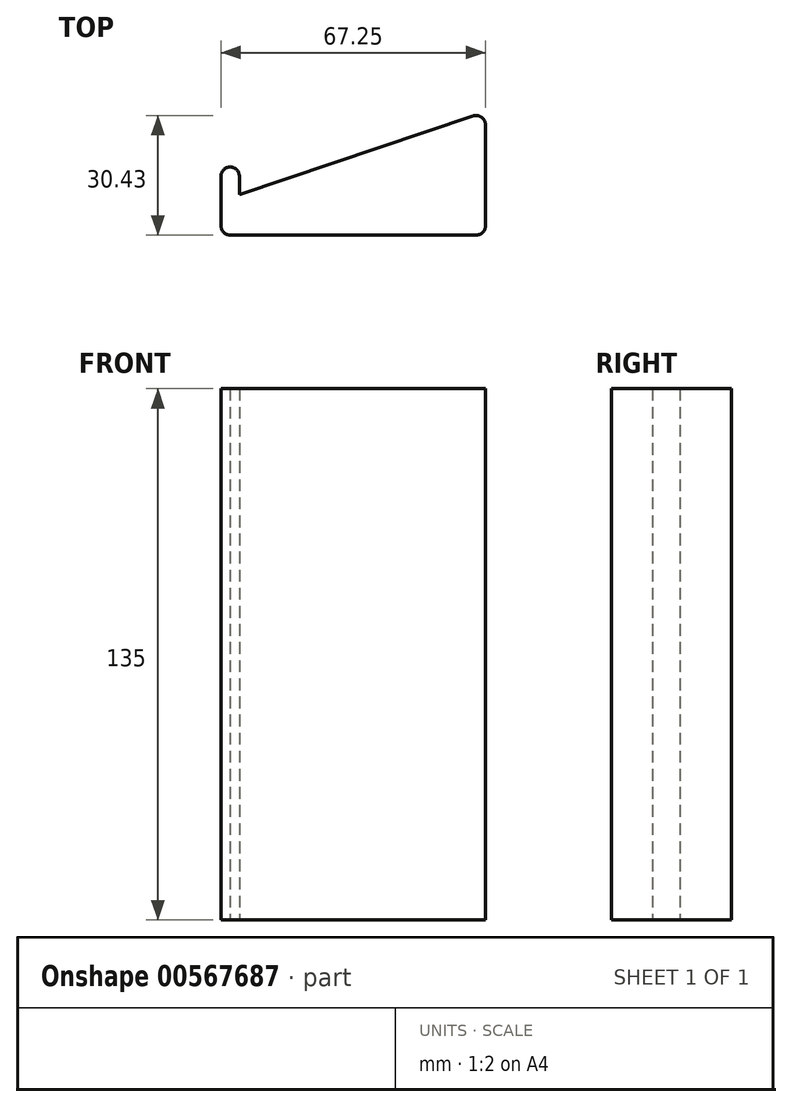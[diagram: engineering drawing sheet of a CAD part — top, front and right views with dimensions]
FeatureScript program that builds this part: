
annotation { "Feature Type Name" : "Feature", "Feature Type Description" : "" }
export const myFeature = defineFeature(function(context is Context, id is Id, definition is map)
    precondition{}
    {
        {
            var Q0;
            Q0=qCreatedBy(makeId("Top.planeOp"),FACE);
            var sketch = newSketch(context, id + "F0", { "sketchPlane" : qUnion([Q0])});
            skLineSegment(sketch, "E0", {"start": v(-28.86, 54.66) * mm, "end": v(30.37, 74.6) * mm});
            skLineSegment(sketch, "E1", {"start": v(33.67, 72.24) * mm, "end": v(33.67, 46.8) * mm});
            skLineSegment(sketch, "E2", {"start": v(31.17, 44.3) * mm, "end": v(-31.08, 44.3) * mm});
            skLineSegment(sketch, "E3", {"start": v(-33.58, 46.8) * mm, "end": v(-33.58, 59.2) * mm});
            skLineSegment(sketch, "E4", {"start": v(-31.36, 61.7) * mm, "end": v(-31.08, 61.7) * mm});
            skLineSegment(sketch, "E5", {"start": v(-28.86, 59.2) * mm, "end": v(-28.86, 54.66) * mm});
            skPoint(sketch, "E6.visualSharp", {"position": v(-28.86, 61.7) * mm});
            skArc(sketch, "E6.filletArc", {"start": v(-28.86, 59.2) * mm, "mid": v(-29.6, 60.96) * mm, "end": v(-31.36, 61.7) * mm});
            skPoint(sketch, "E7.visualSharp", {"position": v(33.67, 75.72) * mm});
            skArc(sketch, "E7.filletArc", {"start": v(33.67, 72.24) * mm, "mid": v(32.63, 74.27) * mm, "end": v(30.37, 74.6) * mm});
            skPoint(sketch, "E8.visualSharp", {"position": v(-33.58, 44.3) * mm});
            skArc(sketch, "E8.filletArc", {"start": v(-33.58, 46.8) * mm, "mid": v(-32.85, 45.04) * mm, "end": v(-31.08, 44.3) * mm});
            skPoint(sketch, "E9.visualSharp", {"position": v(33.67, 44.3) * mm});
            skArc(sketch, "E9.filletArc", {"start": v(31.17, 44.3) * mm, "mid": v(32.94, 45.04) * mm, "end": v(33.67, 46.8) * mm});
            skPoint(sketch, "E10.visualSharp", {"position": v(-33.58, 61.7) * mm});
            skArc(sketch, "E10.filletArc", {"start": v(-31.08, 61.7) * mm, "mid": v(-32.85, 60.96) * mm, "end": v(-33.58, 59.2) * mm});
            skSolve(sketch);
        }
        {
            var Q0;
            Q0=makeQuery(id+"F0.imprint","IMPRINT",FACE,{"disambiguationData":[TD([[makeQuery(id+"F0.imprint","IMPRINT",EDGE,{"derivedFrom":sQuery(id+"F0.wireOp",EDGE,"E0")}),-1.0]])]});
            extrude(context, id + "F1", {"entities" : qUnion([Q0]), "depth" : 135 * mm, "offsetDistance" : 25 * mm});
        }
    });
